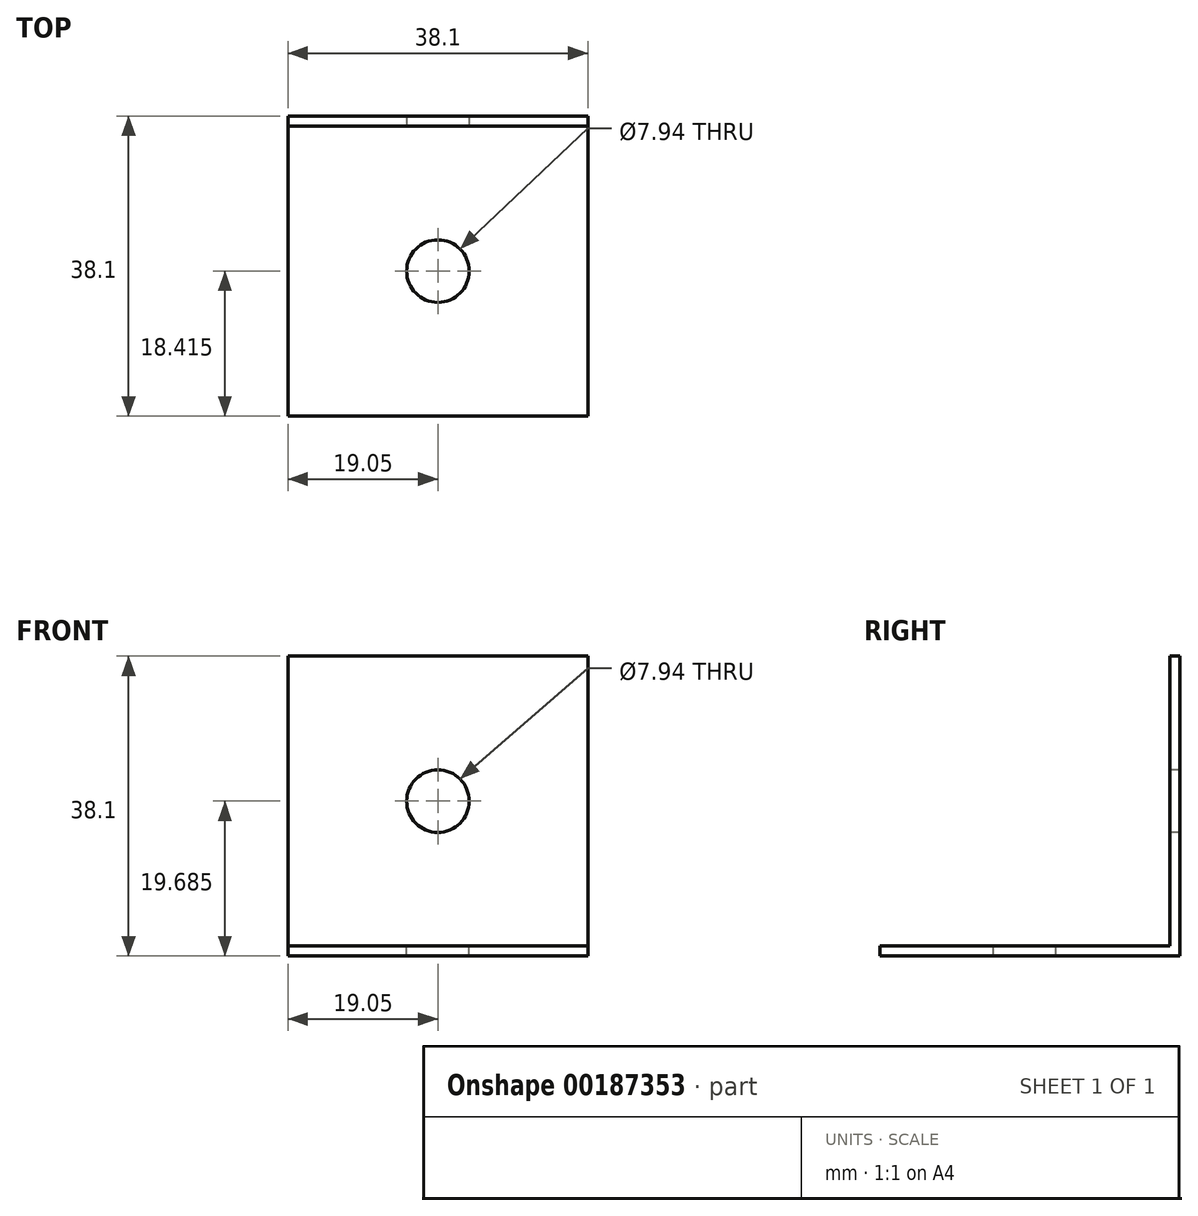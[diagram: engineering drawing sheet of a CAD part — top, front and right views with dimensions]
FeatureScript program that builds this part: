
annotation { "Feature Type Name" : "Feature", "Feature Type Description" : "" }
export const myFeature = defineFeature(function(context is Context, id is Id, definition is map)
    precondition{}
    {
        {
            var Q0;
            Q0=qCreatedBy(makeId("Top.planeOp"),FACE);
            var sketch = newSketch(context, id + "F0", { "sketchPlane" : qUnion([Q0])});
            skLineSegment(sketch, "E0.bottom", {"start": v(-19.05, 19.05) * mm, "end": v(19.05, 19.05) * mm});
            skLineSegment(sketch, "E0.top", {"start": v(-19.05, -19.05) * mm, "end": v(19.05, -19.05) * mm});
            skLineSegment(sketch, "E0.left", {"start": v(-19.05, 19.05) * mm, "end": v(-19.05, -19.05) * mm});
            skLineSegment(sketch, "E0.right", {"start": v(19.05, 19.05) * mm, "end": v(19.05, -19.05) * mm});
            skPoint(sketch, "E0.middle", {"position": v(0, 0) * mm});
            skSolve(sketch);
        }
        {
            var Q0;
            Q0 = qSketchRegion(id + "F0", true);
            extrude(context, id + "F1", {"entities" : qUnion([Q0]), "depth" : 38.1 * mm});
        }
        {
            var Q0;
            Q0=makeQuery(id+"F1.opExtrude","CAP_FACE",FACE,{"disambiguationData":[OSD([sQuery(id+"F0.wireOp",EDGE,"E0.bottom"),sQuery(id+"F0.wireOp",EDGE,"E0.top"),sQuery(id+"F0.wireOp",EDGE,"E0.left"),sQuery(id+"F0.wireOp",EDGE,"E0.right")])],"isStart":false});
            var sketch = newSketch(context, id + "F2", { "sketchPlane" : qUnion([Q0])});
            skLineSegment(sketch, "E1.bottom", {"start": v(19.05, -19.05) * mm, "end": v(-19.05, -19.05) * mm});
            skLineSegment(sketch, "E1.top", {"start": v(19.05, 17.78) * mm, "end": v(-19.05, 17.78) * mm});
            skLineSegment(sketch, "E1.left", {"start": v(19.05, -19.05) * mm, "end": v(19.05, 17.78) * mm});
            skLineSegment(sketch, "E1.right", {"start": v(-19.05, -19.05) * mm, "end": v(-19.05, 17.78) * mm});
            skSolve(sketch);
        }
        {
            var Q0;
            Q0 = qSketchRegion(id + "F2", true);
            extrude(context, id + "F3", {"entities" : qUnion([Q0]), "operationType" : NewBodyOperationType.REMOVE, "oppositeDirection" : true, "depth" : 36.83 * mm});
        }
        {
            var Q0;
            Q0=makeQuery(id+"F3.boolean.opBoolean","COPY",FACE,{"derivedFrom":makeQuery(id+"F3.opExtrude","SWEPT_FACE",FACE,{"disambiguationData":[OSD([sQuery(id+"F2.wireOp",EDGE,"E1.top")])]})});
            var sketch = newSketch(context, id + "F4", { "sketchPlane" : qUnion([Q0])});
            skLineSegment(sketch, "E2", {"start": v(0, 38.1) * mm, "end": v(0, 1.27) * mm});
            skCircle(sketch, "E3", {"center": v(0, 19.69) * mm, "radius": 3.97 * mm});
            skSolve(sketch);
        }
        {
            var Q0;
            Q0=makeQuery(id+"F3.boolean.opBoolean","COPY",FACE,{"derivedFrom":makeQuery(id+"F3.opExtrude","CAP_FACE",FACE,{"disambiguationData":[OSD([sQuery(id+"F2.wireOp",EDGE,"E1.bottom"),sQuery(id+"F2.wireOp",EDGE,"E1.top"),sQuery(id+"F2.wireOp",EDGE,"E1.left"),sQuery(id+"F2.wireOp",EDGE,"E1.right")])],"isStart":false})});
            var sketch = newSketch(context, id + "F5", { "sketchPlane" : qUnion([Q0])});
            skLineSegment(sketch, "E4", {"start": v(0, 17.78) * mm, "end": v(0, -19.05) * mm});
            skPoint(sketch, "E5", {"position": v(0, -0.63) * mm});
            skCircle(sketch, "E6", {"center": v(0, -0.63) * mm, "radius": 3.97 * mm});
            skSolve(sketch);
        }
        {
            var Q0;
            Q0 = qSketchRegion(id + "F4", true);
            extrude(context, id + "F6", {"entities" : qUnion([Q0]), "operationType" : NewBodyOperationType.REMOVE, "oppositeDirection" : true, "depth" : 3.8 * mm});
        }
        {
            var Q0;
            Q0 = qSketchRegion(id + "F5", true);
            extrude(context, id + "F7", {"entities" : qUnion([Q0]), "operationType" : NewBodyOperationType.REMOVE, "oppositeDirection" : true, "depth" : 4.83 * mm});
        }
    });
